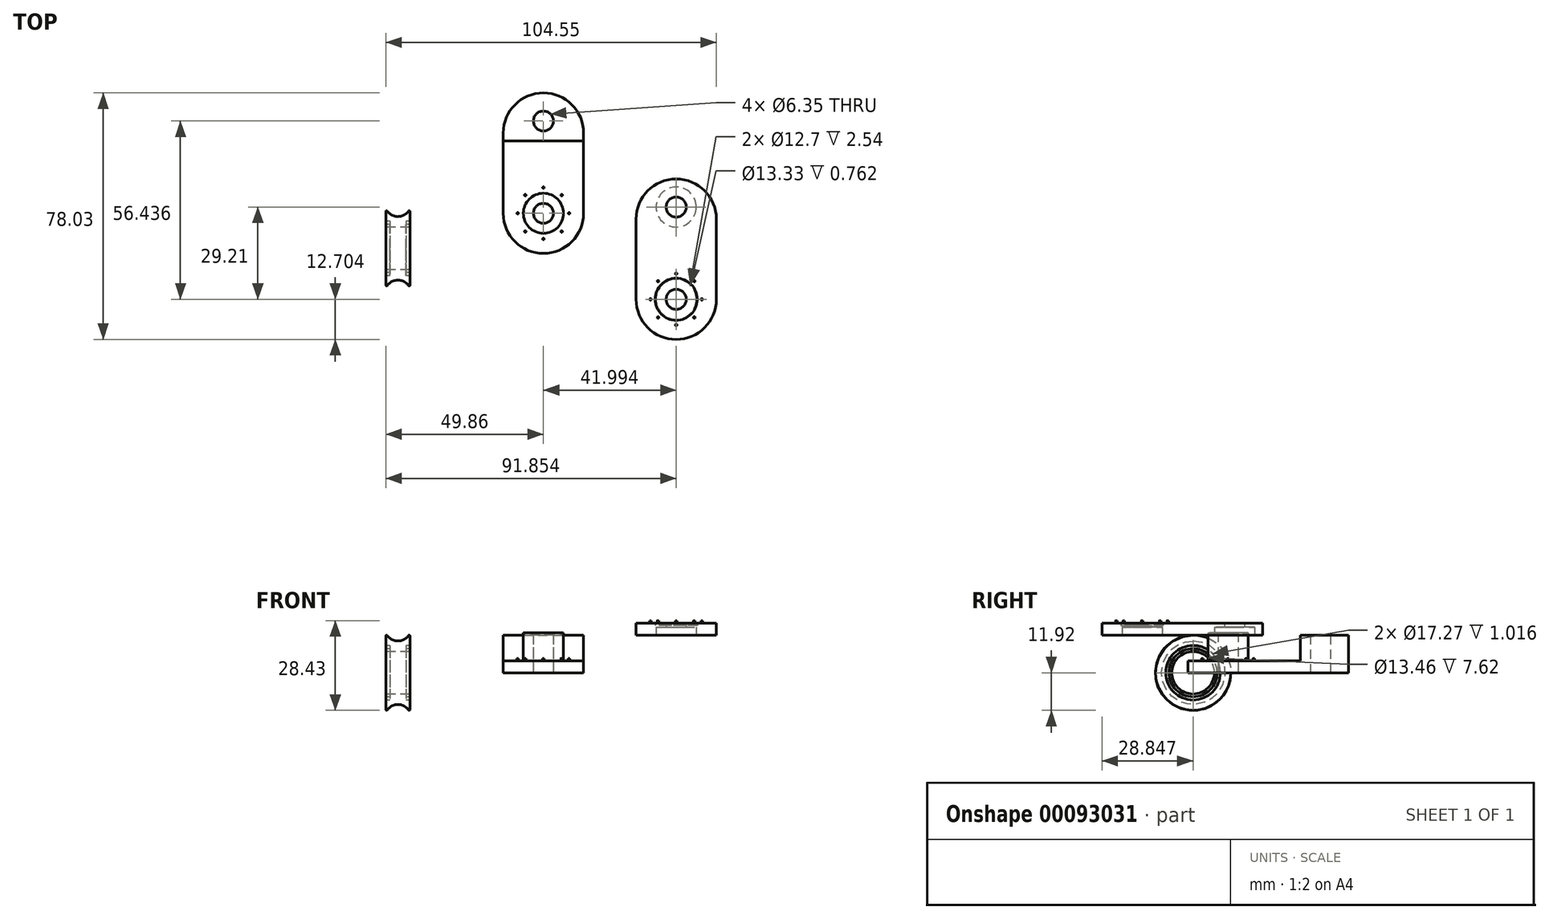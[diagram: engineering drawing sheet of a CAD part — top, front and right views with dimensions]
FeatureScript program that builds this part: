
annotation { "Feature Type Name" : "Feature", "Feature Type Description" : "" }
export const myFeature = defineFeature(function(context is Context, id is Id, definition is map)
    precondition{}
    {
        {
            var Q0;
            Q0=qCreatedBy(makeId("Top.planeOp"),FACE);
            var sketch = newSketch(context, id + "F0", { "sketchPlane" : qUnion([Q0])});
            skLineSegment(sketch, "E0.bottom", {"start": v(0, -25.4) * mm, "end": v(0, -25.4) * mm});
            skLineSegment(sketch, "E0.top", {"start": v(0, 25.4) * mm, "end": v(0, 25.4) * mm});
            skLineSegment(sketch, "E0.left", {"start": v(12.7, -12.7) * mm, "end": v(12.7, 12.7) * mm});
            skLineSegment(sketch, "E0.right", {"start": v(-12.7, -12.7) * mm, "end": v(-12.7, 12.7) * mm});
            skPoint(sketch, "E0.middle", {"position": v(0, 0) * mm});
            skPoint(sketch, "E1.visualSharp", {"position": v(-12.7, 25.4) * mm});
            skArc(sketch, "E1.filletArc", {"start": v(0, 25.4) * mm, "mid": v(-8.98, 21.68) * mm, "end": v(-12.7, 12.7) * mm});
            skPoint(sketch, "E2.visualSharp", {"position": v(12.7, 25.4) * mm});
            skArc(sketch, "E2.filletArc", {"start": v(12.7, 12.7) * mm, "mid": v(8.98, 21.68) * mm, "end": v(0, 25.4) * mm});
            skPoint(sketch, "E3.visualSharp", {"position": v(12.7, -25.4) * mm});
            skArc(sketch, "E3.filletArc", {"start": v(0, -25.4) * mm, "mid": v(8.98, -21.68) * mm, "end": v(12.7, -12.7) * mm});
            skPoint(sketch, "E4.visualSharp", {"position": v(-12.7, -25.4) * mm});
            skArc(sketch, "E4.filletArc", {"start": v(-12.7, -12.7) * mm, "mid": v(-8.98, -21.68) * mm, "end": v(0, -25.4) * mm});
            skCircle(sketch, "E5", {"center": v(0, -12.7) * mm, "radius": 3.18 * mm});
            skPoint(sketch, "E6", {"position": v(0, 2.54) * mm});
            skPoint(sketch, "E7", {"position": v(0, 16.51) * mm});
            skCircle(sketch, "E8", {"center": v(0, 16.51) * mm, "radius": 6.35 * mm});
            skCircle(sketch, "E9", {"center": v(0, 16.51) * mm, "radius": 3.18 * mm});
            skPoint(sketch, "E10", {"position": v(0, 10.16) * mm});
            skLineSegment(sketch, "E11", {"start": v(-12.7, 10.16) * mm, "end": v(12.7, 10.16) * mm});
            skCircle(sketch, "E12", {"center": v(0, -12.7) * mm, "radius": 6.35 * mm});
            skCircle(sketch, "E13", {"center": v(0, -12.7) * mm, "radius": 8.64 * mm, "construction": true});
            skCircle(sketch, "E14", {"center": v(0, -12.7) * mm, "radius": 7.62 * mm, "construction": true});
            skLineSegment(sketch, "E15", {"start": v(0, -4.06) * mm, "end": v(0, -21.34) * mm, "construction": true});
            skLineSegment(sketch, "E16", {"start": v(8.64, -12.7) * mm, "end": v(-8.64, -12.7) * mm, "construction": true});
            skLineSegment(sketch, "E17", {"start": v(0, -12.7) * mm, "end": v(-6.1, -6.6) * mm, "construction": true});
            skLineSegment(sketch, "E18", {"start": v(0, -12.7) * mm, "end": v(6.1, -6.6) * mm, "construction": true});
            skLineSegment(sketch, "E19", {"start": v(0, -12.7) * mm, "end": v(-6.1, -18.8) * mm, "construction": true});
            skLineSegment(sketch, "E20", {"start": v(0, -12.7) * mm, "end": v(6.1, -18.8) * mm, "construction": true});
            skPoint(sketch, "E21", {"position": v(0, -4.57) * mm});
            skPoint(sketch, "E22", {"position": v(-5.75, -6.95) * mm});
            skPoint(sketch, "E23", {"position": v(-8.13, -12.7) * mm});
            skPoint(sketch, "E24", {"position": v(-5.75, -18.45) * mm});
            skPoint(sketch, "E25", {"position": v(0, -20.83) * mm});
            skPoint(sketch, "E26", {"position": v(5.75, -18.45) * mm});
            skPoint(sketch, "E27", {"position": v(8.13, -12.7) * mm});
            skPoint(sketch, "E28", {"position": v(5.75, -6.95) * mm});
            skCircle(sketch, "E29", {"center": v(-5.75, -6.95) * mm, "radius": 0.25 * mm});
            skCircle(sketch, "E30", {"center": v(-8.13, -12.7) * mm, "radius": 0.25 * mm});
            skCircle(sketch, "E31", {"center": v(-5.75, -18.45) * mm, "radius": 0.25 * mm});
            skCircle(sketch, "E32", {"center": v(0, -20.83) * mm, "radius": 0.25 * mm});
            skCircle(sketch, "E33", {"center": v(5.75, -18.45) * mm, "radius": 0.25 * mm});
            skCircle(sketch, "E34", {"center": v(8.13, -12.7) * mm, "radius": 0.25 * mm});
            skCircle(sketch, "E35", {"center": v(5.75, -6.95) * mm, "radius": 0.25 * mm});
            skCircle(sketch, "E36", {"center": v(0, -4.57) * mm, "radius": 0.25 * mm});
            skSolve(sketch);
        }
        {
            var Q0;
            {var subQ1=sQuery(id+"F0.wireOp",EDGE,"E3.filletArc");Q0=makeQuery(id+"F0.imprint","IMPRINT",FACE,{"disambiguationData":[TD([[makeQuery(id+"F0.imprint","IMPRINT",EDGE,{"derivedFrom":subQ1}),1.0]])]});}
            extrude(context, id + "F1", {"entities" : qUnion([Q0]), "depth" : 3.8 * mm});
        }
        {
            var Q0;
            {var subQ6=sQuery(id+"F0.wireOp",EDGE,"E1.filletArc");Q0=makeQuery(id+"F0.imprint","IMPRINT",FACE,{"disambiguationData":[TD([[makeQuery(id+"F0.imprint","IMPRINT",EDGE,{"derivedFrom":subQ6}),1.0]])]});}
            var Q1;
            Q1=makeQuery(id+"F0.imprint","IMPRINT",FACE,{"disambiguationData":[TD([[makeQuery(id+"F0.imprint","IMPRINT",EDGE,{"derivedFrom":sQuery(id+"F0.wireOp",EDGE,"E8")}),1.0]])]});
            extrude(context, id + "F2", {"entities" : qUnion([Q0, Q1]), "operationType" : NewBodyOperationType.ADD, "depth" : 11.94 * mm});
        }
        {
            var Q0;
            Q0=makeQuery(id+"F0.imprint","IMPRINT",FACE,{"disambiguationData":[TD([[makeQuery(id+"F0.imprint","IMPRINT",EDGE,{"derivedFrom":sQuery(id+"F0.wireOp",EDGE,"E30")}),1.0]])]});
            var Q1;
            Q1=makeQuery(id+"F0.imprint","IMPRINT",FACE,{"disambiguationData":[TD([[makeQuery(id+"F0.imprint","IMPRINT",EDGE,{"derivedFrom":sQuery(id+"F0.wireOp",EDGE,"E31")}),1.0]])]});
            var Q2;
            Q2=makeQuery(id+"F0.imprint","IMPRINT",FACE,{"disambiguationData":[TD([[makeQuery(id+"F0.imprint","IMPRINT",EDGE,{"derivedFrom":sQuery(id+"F0.wireOp",EDGE,"E32")}),1.0]])]});
            var Q3;
            Q3=makeQuery(id+"F0.imprint","IMPRINT",FACE,{"disambiguationData":[TD([[makeQuery(id+"F0.imprint","IMPRINT",EDGE,{"derivedFrom":sQuery(id+"F0.wireOp",EDGE,"E33")}),1.0]])]});
            var Q4;
            Q4=makeQuery(id+"F0.imprint","IMPRINT",FACE,{"disambiguationData":[TD([[makeQuery(id+"F0.imprint","IMPRINT",EDGE,{"derivedFrom":sQuery(id+"F0.wireOp",EDGE,"E34")}),1.0]])]});
            var Q5;
            Q5=makeQuery(id+"F0.imprint","IMPRINT",FACE,{"disambiguationData":[TD([[makeQuery(id+"F0.imprint","IMPRINT",EDGE,{"derivedFrom":sQuery(id+"F0.wireOp",EDGE,"E35")}),1.0]])]});
            var Q6;
            Q6=makeQuery(id+"F0.imprint","IMPRINT",FACE,{"disambiguationData":[TD([[makeQuery(id+"F0.imprint","IMPRINT",EDGE,{"derivedFrom":sQuery(id+"F0.wireOp",EDGE,"E36")}),1.0]])]});
            var Q7;
            Q7=makeQuery(id+"F0.imprint","IMPRINT",FACE,{"disambiguationData":[TD([[makeQuery(id+"F0.imprint","IMPRINT",EDGE,{"derivedFrom":sQuery(id+"F0.wireOp",EDGE,"E29")}),1.0]])]});
            extrude(context, id + "F3", {"entities" : qUnion([Q0, Q1, Q2, Q3, Q4, Q5, Q6, Q7]), "operationType" : NewBodyOperationType.ADD, "depth" : 4.57 * mm});
        }
        {
            var Q0;
            Q0=qCreatedBy(makeId("Top.planeOp"),FACE);
            var sketch = newSketch(context, id + "F4", { "sketchPlane" : qUnion([Q0])});
            skLineSegment(sketch, "E37", {"start": v(-42.24, -12.12) * mm, "end": v(-42.24, -14.9) * mm});
            skLineSegment(sketch, "E38", {"start": v(-49.86, -12.12) * mm, "end": v(-49.86, -14.9) * mm});
            skPoint(sketch, "E39", {"position": v(-49.86, -17.05) * mm});
            skPoint(sketch, "E40", {"position": v(-49.86, -16.16) * mm});
            skPoint(sketch, "E41", {"position": v(-49.86, -15.15) * mm});
            skArc(sketch, "E42", {"start": v(-49.4, -11.97) * mm, "mid": v(-46.05, -13.73) * mm, "end": v(-42.7, -11.97) * mm});
            skPoint(sketch, "E43.visualSharp", {"position": v(-49.86, -11.08) * mm});
            skArc(sketch, "E43.filletArc", {"start": v(-49.4, -11.97) * mm, "mid": v(-49.68, -11.88) * mm, "end": v(-49.86, -12.12) * mm});
            skPoint(sketch, "E44.visualSharp", {"position": v(-42.24, -11.08) * mm});
            skArc(sketch, "E44.filletArc", {"start": v(-42.24, -12.12) * mm, "mid": v(-42.42, -11.88) * mm, "end": v(-42.7, -11.97) * mm});
            skLineSegment(sketch, "E45", {"start": v(-49.86, -17.05) * mm, "end": v(-42.24, -17.05) * mm});
            skLineSegment(sketch, "E46", {"start": v(-49.6, -16.16) * mm, "end": v(-42.5, -16.16) * mm});
            skLineSegment(sketch, "E47", {"start": v(-49.6, -15.15) * mm, "end": v(-42.5, -15.15) * mm});
            skPoint(sketch, "E48", {"position": v(-48.59, -15.15) * mm});
            skPoint(sketch, "E49", {"position": v(-43.5, -15.15) * mm});
            skLineSegment(sketch, "E50", {"start": v(-48.59, -15.15) * mm, "end": v(-48.59, -16.16) * mm});
            skLineSegment(sketch, "E51", {"start": v(-43.5, -15.15) * mm, "end": v(-43.5, -16.16) * mm});
            skLineSegment(sketch, "E52.trimOffspring", {"start": v(-49.86, -16.42) * mm, "end": v(-49.86, -23.78) * mm});
            skLineSegment(sketch, "E53.trimOffspring", {"start": v(-42.24, -16.42) * mm, "end": v(-42.24, -23.78) * mm});
            skArc(sketch, "E54.filletArc", {"start": v(-49.86, -14.9) * mm, "mid": v(-49.78, -15.07) * mm, "end": v(-49.6, -15.15) * mm});
            skArc(sketch, "E55.filletArc", {"start": v(-49.6, -16.16) * mm, "mid": v(-49.78, -16.24) * mm, "end": v(-49.86, -16.42) * mm});
            skPoint(sketch, "E56.visualSharp", {"position": v(-42.24, -16.16) * mm});
            skArc(sketch, "E56.filletArc", {"start": v(-42.24, -16.42) * mm, "mid": v(-42.31, -16.24) * mm, "end": v(-42.5, -16.16) * mm});
            skPoint(sketch, "E57.visualSharp", {"position": v(-42.24, -15.15) * mm});
            skArc(sketch, "E57.filletArc", {"start": v(-42.5, -15.15) * mm, "mid": v(-42.31, -15.07) * mm, "end": v(-42.24, -14.9) * mm});
            skLineSegment(sketch, "E58", {"start": v(-49.86, -23.78) * mm, "end": v(-42.24, -23.78) * mm});
            skSolve(sketch);
        }
        {
            var Q0;
            Q0=makeQuery(id+"F4.imprint","IMPRINT",FACE,{"disambiguationData":[TD([[makeQuery(id+"F4.imprint","IMPRINT",EDGE,{"derivedFrom":sQuery(id+"F4.wireOp",EDGE,"E37")}),-1.0]])]});
            var Q1;
            {var subQ0=sQuery(id+"F4.wireOp",EDGE,"E50");Q1=makeQuery(id+"F4.imprint","IMPRINT",FACE,{"disambiguationData":[TD([[makeQuery(id+"F4.imprint","IMPRINT",EDGE,{"derivedFrom":subQ0}),1.0]])]});}
            var Q2;
            {var subQ5=sQuery(id+"F4.wireOp",EDGE,"E45");Q2=makeQuery(id+"F4.imprint","IMPRINT",FACE,{"disambiguationData":[TD([[makeQuery(id+"F4.imprint","IMPRINT",EDGE,{"derivedFrom":subQ5}),1.0]])]});}
            var Q3;
            Q3=sQuery(id+"F4.wireOp",EDGE,"E58");
            revolve(context, id + "F5", {"entities" : qUnion([Q0, Q1, Q2]), "axis" : qUnion([Q3]), "revolveType" : RevolveType.FULL});
        }
        {
            var Q0;
            Q0=makeQuery(id+"F2.opExtrude","CAP_FACE",FACE,{"disambiguationData":[OSD([sQuery(id+"F0.wireOp",EDGE,"E0.left"),sQuery(id+"F0.wireOp",EDGE,"E0.right"),sQuery(id+"F0.wireOp",EDGE,"E1.filletArc"),sQuery(id+"F0.wireOp",EDGE,"E2.filletArc"),sQuery(id+"F0.wireOp",EDGE,"E9"),sQuery(id+"F0.wireOp",EDGE,"E11")])],"isStart":false});
            var sketch = newSketch(context, id + "F6", { "sketchPlane" : qUnion([Q0])});
            skLineSegment(sketch, "E59.bottom", {"start": v(42, -52.63) * mm, "end": v(42, -52.63) * mm});
            skLineSegment(sketch, "E59.top", {"start": v(42, -1.83) * mm, "end": v(42, -1.83) * mm});
            skLineSegment(sketch, "E59.left", {"start": v(54.7, -39.93) * mm, "end": v(54.7, -14.53) * mm});
            skLineSegment(sketch, "E59.right", {"start": v(29.3, -39.93) * mm, "end": v(29.3, -14.53) * mm});
            skPoint(sketch, "E59.middle", {"position": v(42, -27.23) * mm});
            skPoint(sketch, "E60.visualSharp", {"position": v(29.3, -1.83) * mm});
            skArc(sketch, "E60.filletArc", {"start": v(42, -1.83) * mm, "mid": v(33.01, -5.55) * mm, "end": v(29.3, -14.53) * mm});
            skPoint(sketch, "E61.visualSharp", {"position": v(54.7, -1.83) * mm});
            skArc(sketch, "E61.filletArc", {"start": v(54.7, -14.53) * mm, "mid": v(50.97, -5.55) * mm, "end": v(42, -1.83) * mm});
            skPoint(sketch, "E62.visualSharp", {"position": v(54.7, -52.63) * mm});
            skArc(sketch, "E62.filletArc", {"start": v(42, -52.63) * mm, "mid": v(50.97, -48.9) * mm, "end": v(54.7, -39.93) * mm});
            skPoint(sketch, "E63.visualSharp", {"position": v(29.3, -52.63) * mm});
            skArc(sketch, "E63.filletArc", {"start": v(29.3, -39.93) * mm, "mid": v(33.01, -48.9) * mm, "end": v(42, -52.63) * mm});
            skPoint(sketch, "E64", {"position": v(42, -24.69) * mm});
            skPoint(sketch, "E65", {"position": v(42, -10.72) * mm});
            skCircle(sketch, "E66", {"center": v(42, -10.72) * mm, "radius": 3.18 * mm});
            skPoint(sketch, "E67", {"position": v(42, -17.07) * mm});
            skCircle(sketch, "E68", {"center": v(42, -39.93) * mm, "radius": 3.18 * mm});
            skCircle(sketch, "E69", {"center": v(42, -39.93) * mm, "radius": 6.67 * mm});
            skCircle(sketch, "E70", {"center": v(42, -39.93) * mm, "radius": 8.64 * mm, "construction": true});
            skCircle(sketch, "E71", {"center": v(42, -39.93) * mm, "radius": 7.62 * mm, "construction": true});
            skLineSegment(sketch, "E72", {"start": v(42, -31.3) * mm, "end": v(42, -48.56) * mm, "construction": true});
            skLineSegment(sketch, "E73", {"start": v(50.63, -39.93) * mm, "end": v(33.36, -39.93) * mm, "construction": true});
            skLineSegment(sketch, "E74", {"start": v(42.6, -40.53) * mm, "end": v(35.89, -33.82) * mm, "construction": true});
            skLineSegment(sketch, "E75", {"start": v(47.18, -34.74) * mm, "end": v(48.1, -33.82) * mm, "construction": true});
            skLineSegment(sketch, "E76", {"start": v(47.18, -34.74) * mm, "end": v(35.89, -46.03) * mm, "construction": true});
            skLineSegment(sketch, "E77", {"start": v(42.6, -40.53) * mm, "end": v(48.1, -46.03) * mm, "construction": true});
            skPoint(sketch, "E78", {"position": v(42, -31.8) * mm});
            skPoint(sketch, "E79", {"position": v(36.25, -34.18) * mm});
            skPoint(sketch, "E80", {"position": v(33.87, -39.93) * mm});
            skPoint(sketch, "E81", {"position": v(36.25, -45.67) * mm});
            skPoint(sketch, "E82", {"position": v(47.74, -45.67) * mm});
            skPoint(sketch, "E83", {"position": v(50.12, -39.93) * mm});
            skPoint(sketch, "E84", {"position": v(47.74, -34.18) * mm});
            skCircle(sketch, "E85", {"center": v(36.25, -34.18) * mm, "radius": 0.25 * mm});
            skCircle(sketch, "E86", {"center": v(33.87, -39.93) * mm, "radius": 0.25 * mm});
            skCircle(sketch, "E87", {"center": v(36.25, -45.67) * mm, "radius": 0.25 * mm});
            skCircle(sketch, "E88", {"center": v(47.74, -45.67) * mm, "radius": 0.25 * mm});
            skCircle(sketch, "E89", {"center": v(50.12, -39.93) * mm, "radius": 0.25 * mm});
            skCircle(sketch, "E90", {"center": v(47.74, -34.18) * mm, "radius": 0.25 * mm});
            skCircle(sketch, "E91", {"center": v(42, -31.8) * mm, "radius": 0.25 * mm});
            skPoint(sketch, "E92", {"position": v(42, -48.05) * mm});
            skCircle(sketch, "E93", {"center": v(42, -48.05) * mm, "radius": 0.25 * mm});
            skSolve(sketch);
        }
        {
            var Q0;
            {var subQ5=sQuery(id+"F6.wireOp",EDGE,"E59.left");Q0=makeQuery(id+"F6.imprint","IMPRINT",FACE,{"disambiguationData":[TD([[makeQuery(id+"F6.imprint","IMPRINT",EDGE,{"derivedFrom":subQ5}),1.0]])]});}
            var Q1;
            {var subQ5=sQuery(id+"F6.wireOp",EDGE,"E60.filletArc");Q1=makeQuery(id+"F6.imprint","IMPRINT",FACE,{"disambiguationData":[TD([[makeQuery(id+"F6.imprint","IMPRINT",EDGE,{"derivedFrom":subQ5}),1.0]])]});}
            var Q2;
            Q2=makeQuery(id+"F6.imprint","IMPRINT",FACE,{"disambiguationData":[TD([[makeQuery(id+"F6.imprint","IMPRINT",EDGE,{"derivedFrom":sQuery(id+"F6.wireOp",EDGE,"E66")}),1.0]])]});
            extrude(context, id + "F7", {"entities" : qUnion([Q0, Q1, Q2]), "operationType" : NewBodyOperationType.ADD, "depth" : 3.8 * mm});
        }
        {
            var Q0;
            Q0=makeQuery(id+"F6.imprint","IMPRINT",FACE,{"disambiguationData":[TD([[makeQuery(id+"F6.imprint","IMPRINT",EDGE,{"derivedFrom":sQuery(id+"F6.wireOp",EDGE,"E91")}),1.0]])]});
            var Q1;
            Q1=makeQuery(id+"F6.imprint","IMPRINT",FACE,{"disambiguationData":[TD([[makeQuery(id+"F6.imprint","IMPRINT",EDGE,{"derivedFrom":sQuery(id+"F6.wireOp",EDGE,"E85")}),1.0]])]});
            var Q2;
            Q2=makeQuery(id+"F6.imprint","IMPRINT",FACE,{"disambiguationData":[TD([[makeQuery(id+"F6.imprint","IMPRINT",EDGE,{"derivedFrom":sQuery(id+"F6.wireOp",EDGE,"E86")}),1.0]])]});
            var Q3;
            Q3=makeQuery(id+"F6.imprint","IMPRINT",FACE,{"disambiguationData":[TD([[makeQuery(id+"F6.imprint","IMPRINT",EDGE,{"derivedFrom":sQuery(id+"F6.wireOp",EDGE,"E90")}),1.0]])]});
            var Q4;
            Q4=makeQuery(id+"F6.imprint","IMPRINT",FACE,{"disambiguationData":[TD([[makeQuery(id+"F6.imprint","IMPRINT",EDGE,{"derivedFrom":sQuery(id+"F6.wireOp",EDGE,"E89")}),1.0]])]});
            var Q5;
            Q5=makeQuery(id+"F6.imprint","IMPRINT",FACE,{"disambiguationData":[TD([[makeQuery(id+"F6.imprint","IMPRINT",EDGE,{"derivedFrom":sQuery(id+"F6.wireOp",EDGE,"E88")}),1.0]])]});
            var Q6;
            Q6=makeQuery(id+"F6.imprint","IMPRINT",FACE,{"disambiguationData":[TD([[makeQuery(id+"F6.imprint","IMPRINT",EDGE,{"derivedFrom":sQuery(id+"F6.wireOp",EDGE,"E87")}),1.0]])]});
            var Q7;
            Q7=makeQuery(id+"F6.imprint","IMPRINT",FACE,{"disambiguationData":[TD([[makeQuery(id+"F6.imprint","IMPRINT",EDGE,{"derivedFrom":sQuery(id+"F6.wireOp",EDGE,"E93")}),1.0]])]});
            extrude(context, id + "F8", {"entities" : qUnion([Q0, Q1, Q2, Q3, Q4, Q5, Q6, Q7]), "operationType" : NewBodyOperationType.ADD, "depth" : 4.57 * mm});
        }
        {
            var Q0;
            Q0=makeQuery(id+"F0.imprint","IMPRINT",FACE,{"disambiguationData":[TD([[makeQuery(id+"F0.imprint","IMPRINT",EDGE,{"derivedFrom":sQuery(id+"F0.wireOp",EDGE,"E5")}),-1.0]])]});
            extrude(context, id + "F9", {"entities" : qUnion([Q0]), "operationType" : NewBodyOperationType.ADD, "depth" : 12.7 * mm});
        }
        {
            var Q0;
            Q0=makeQuery(id+"F6.imprint","IMPRINT",FACE,{"disambiguationData":[TD([[makeQuery(id+"F6.imprint","IMPRINT",EDGE,{"derivedFrom":sQuery(id+"F6.wireOp",EDGE,"E68")}),-1.0]])]});
            var Q1;
            Q1=makeQuery(id+"F6.imprint","IMPRINT",FACE,{"disambiguationData":[TD([[makeQuery(id+"F6.imprint","IMPRINT",EDGE,{"derivedFrom":sQuery(id+"F6.wireOp",EDGE,"E68")}),1.0]])]});
            extrude(context, id + "F10", {"entities" : qUnion([Q0, Q1]), "operationType" : NewBodyOperationType.ADD, "depth" : 3.05 * mm});
        }
        {
            var Q0;
            Q0=sQuery(id+"F6.wireOp",VERTEX,"E62.filletArc.center");
            var Q1;
            Q1=sQuery(id+"F6.wireOp",VERTEX,"E65");
            var Q2;
            Q2=makeQuery(id+"F7.opExtrude","SWEPT_BODY",BODY,{"disambiguationData":[OSD([sQuery(id+"F6.wireOp",EDGE,"E59.left"),sQuery(id+"F6.wireOp",EDGE,"E59.right"),sQuery(id+"F6.wireOp",EDGE,"E60.filletArc"),sQuery(id+"F6.wireOp",EDGE,"E61.filletArc"),sQuery(id+"F6.wireOp",EDGE,"E62.filletArc"),sQuery(id+"F6.wireOp",EDGE,"E63.filletArc"),sQuery(id+"F6.wireOp",EDGE,"E69"),sQuery(id+"F6.wireOp",EDGE,"E85"),sQuery(id+"F6.wireOp",EDGE,"E86"),sQuery(id+"F6.wireOp",EDGE,"E87"),sQuery(id+"F6.wireOp",EDGE,"E88"),sQuery(id+"F6.wireOp",EDGE,"E89"),sQuery(id+"F6.wireOp",EDGE,"E90"),sQuery(id+"F6.wireOp",EDGE,"E91"),sQuery(id+"F6.wireOp",EDGE,"E93")])]});
            hole(context, id + "F11", {"style" : HoleStyle.C_BORE, "endStyle" : HoleEndStyle.THROUGH, "oppositeDirection" : true, "holeDiameter" : 6.35 * mm, "cBoreDiameter" : 12.7 * mm, "cBoreDepth" : 2.54 * mm, "locations" : qUnion([Q0, Q1]), "scope" : qUnion([Q2]), "isTappedThrough" : true});
        }
    });
